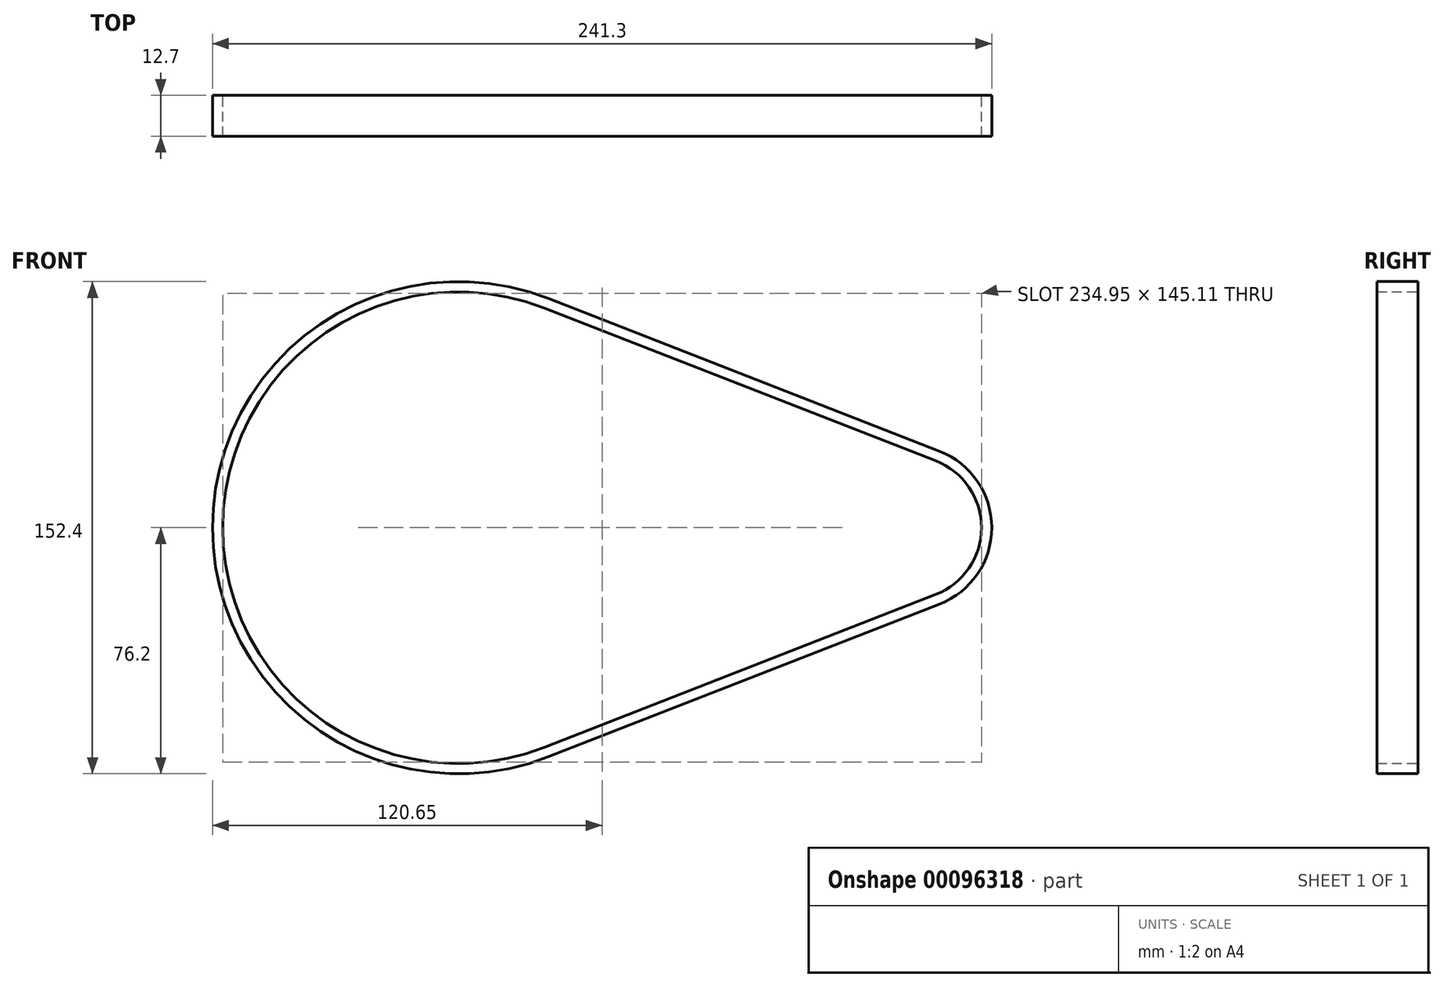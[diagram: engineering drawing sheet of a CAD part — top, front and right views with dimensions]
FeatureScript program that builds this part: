
annotation { "Feature Type Name" : "Feature", "Feature Type Description" : "" }
export const myFeature = defineFeature(function(context is Context, id is Id, definition is map)
    precondition{}
    {
        {
            var Q0;
            Q0=qCreatedBy(makeId("Front.planeOp"),FACE);
            var sketch = newSketch(context, id + "F0", { "sketchPlane" : qUnion([Q0])});
            skArc(sketch, "E0", {"start": v(27.7, 70.98) * mm, "mid": v(-76.2, 0) * mm, "end": v(27.7, -70.98) * mm});
            skArc(sketch, "E1", {"start": v(148.94, -23.66) * mm, "mid": v(165.1, 0) * mm, "end": v(148.94, 23.66) * mm});
            skLineSegment(sketch, "E2", {"start": v(27.7, 70.98) * mm, "end": v(148.94, 23.66) * mm});
            skLineSegment(sketch, "E3", {"start": v(27.7, -70.98) * mm, "end": v(148.94, -23.66) * mm});
            skLineSegment(sketch, "E4.0", {"start": v(26.55, -68.03) * mm, "end": v(147.78, -20.7) * mm});
            skArc(sketch, "E5.0", {"start": v(26.55, 68.03) * mm, "mid": v(-73.03, 0) * mm, "end": v(26.55, -68.03) * mm});
            skArc(sketch, "E6.0", {"start": v(147.78, -20.7) * mm, "mid": v(161.93, 0) * mm, "end": v(147.78, 20.7) * mm});
            skLineSegment(sketch, "E7.0", {"start": v(26.55, 68.03) * mm, "end": v(147.78, 20.7) * mm});
            skSolve(sketch);
        }
        {
            var Q0;
            Q0 = qSketchRegion(id + "F0", true);
            extrude(context, id + "F1", {"entities" : qUnion([Q0]), "depth" : 12.7 * mm});
        }
    });
